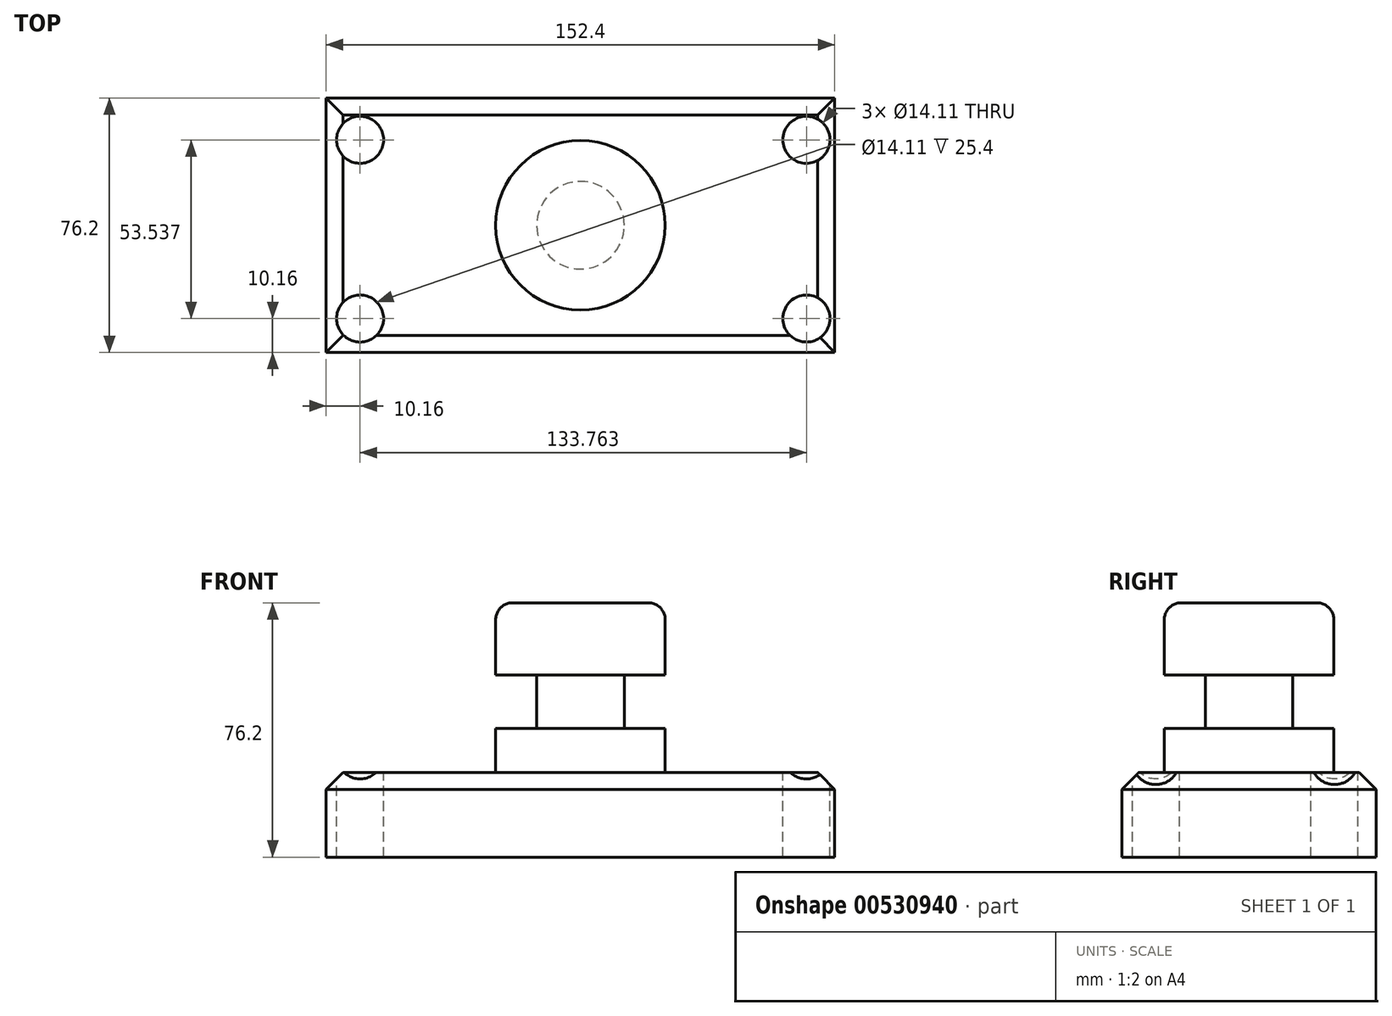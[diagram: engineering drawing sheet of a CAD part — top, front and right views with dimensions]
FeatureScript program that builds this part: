
annotation { "Feature Type Name" : "Feature", "Feature Type Description" : "" }
export const myFeature = defineFeature(function(context is Context, id is Id, definition is map)
    precondition{}
    {
        {
            var Q0;
            Q0=qCreatedBy(makeId("Top.planeOp"),FACE);
            var sketch = newSketch(context, id + "F0", { "sketchPlane" : qUnion([Q0])});
            skLineSegment(sketch, "E0.bottom", {"start": v(-76.2, 38.1) * mm, "end": v(76.2, 38.1) * mm});
            skLineSegment(sketch, "E0.top", {"start": v(-76.2, -38.1) * mm, "end": v(76.2, -38.1) * mm});
            skLineSegment(sketch, "E0.left", {"start": v(-76.2, 38.1) * mm, "end": v(-76.2, -38.1) * mm});
            skLineSegment(sketch, "E0.right", {"start": v(76.2, 38.1) * mm, "end": v(76.2, -38.1) * mm});
            skPoint(sketch, "E0.middle", {"position": v(0, 0) * mm});
            skSolve(sketch);
        }
        {
            var Q0;
            Q0=makeQuery(id+"F0.imprint","IMPRINT",FACE,{"disambiguationData":[TD([[makeQuery(id+"F0.imprint","IMPRINT",EDGE,{"derivedFrom":sQuery(id+"F0.wireOp",EDGE,"E0.bottom")}),-1.0]])]});
            extrude(context, id + "F1", {"entities" : qUnion([Q0]), "depth" : 25.4 * mm, "offsetDistance" : 25.4 * mm});
        }
        {
            var Q0;
            Q0=makeQuery(id+"F1.opExtrude","CAP_FACE",FACE,{"disambiguationData":[OSD([sQuery(id+"F0.wireOp",EDGE,"E0.bottom"),sQuery(id+"F0.wireOp",EDGE,"E0.top"),sQuery(id+"F0.wireOp",EDGE,"E0.left"),sQuery(id+"F0.wireOp",EDGE,"E0.right")])],"isStart":false});
            var sketch = newSketch(context, id + "F2", { "sketchPlane" : qUnion([Q0])});
            skCircle(sketch, "E1", {"center": v(67.72, 25.6) * mm, "radius": 7.05 * mm});
            skCircle(sketch, "E2", {"center": v(-66.04, 25.6) * mm, "radius": 7.05 * mm});
            skCircle(sketch, "E3", {"center": v(-66.04, -27.94) * mm, "radius": 7.05 * mm});
            skCircle(sketch, "E4", {"center": v(67.72, -27.94) * mm, "radius": 7.05 * mm});
            skSolve(sketch);
        }
        {
            var Q0;
            Q0 = qSketchRegion(id + "F2", true);
            extrude(context, id + "F3", {"entities" : qUnion([Q0]), "operationType" : NewBodyOperationType.REMOVE, "endBound" : BoundingType.THROUGH_ALL, "oppositeDirection" : true, "depth" : 25.4 * mm, "offsetDistance" : 25.4 * mm});
        }
        {
            var Q0;
            Q0=qCreatedBy(makeId("Front.planeOp"),FACE);
            var sketch = newSketch(context, id + "F4", { "sketchPlane" : qUnion([Q0])});
            skLineSegment(sketch, "E5.bottom", {"start": v(0, 25.4) * mm, "end": v(25.4, 25.4) * mm});
            skLineSegment(sketch, "E5.top", {"start": v(0, 76.2) * mm, "end": v(25.4, 76.2) * mm});
            skLineSegment(sketch, "E5.left", {"start": v(0, 25.4) * mm, "end": v(0, 76.2) * mm});
            skLineSegment(sketch, "E5.right", {"start": v(25.4, 25.4) * mm, "end": v(25.4, 76.2) * mm});
            skSolve(sketch);
        }
        {
            var Q0;
            Q0=makeQuery(id+"F4.imprint","IMPRINT",FACE,{"disambiguationData":[TD([[makeQuery(id+"F4.imprint","IMPRINT",EDGE,{"derivedFrom":sQuery(id+"F4.wireOp",EDGE,"E5.bottom")}),1.0]])]});
            var Q1;
            Q1=sQuery(id+"F4.wireOp",EDGE,"E5.left");
            revolve(context, id + "F5", {"operationType" : NewBodyOperationType.ADD, "entities" : qUnion([Q0]), "axis" : qUnion([Q1]), "revolveType" : RevolveType.FULL});
        }
        {
            var Q0;
            Q0=qCreatedBy(makeId("Front.planeOp"),FACE);
            var sketch = newSketch(context, id + "F6", { "sketchPlane" : qUnion([Q0])});
            skLineSegment(sketch, "E6.bottom", {"start": v(31.35, 54.56) * mm, "end": v(13.12, 54.56) * mm});
            skLineSegment(sketch, "E6.top", {"start": v(31.35, 38.53) * mm, "end": v(13.12, 38.53) * mm});
            skLineSegment(sketch, "E6.left", {"start": v(31.35, 54.56) * mm, "end": v(31.35, 38.53) * mm});
            skLineSegment(sketch, "E6.right", {"start": v(13.12, 54.56) * mm, "end": v(13.12, 38.53) * mm});
            skSolve(sketch);
        }
        {
            var Q0;
            Q0=qCreatedBy(makeId("Right.planeOp"),FACE);
            var sketch = newSketch(context, id + "F7", { "sketchPlane" : qUnion([Q0])});
            skLineSegment(sketch, "E7", {"start": v(0, 0) * mm, "end": v(0, 64.5) * mm});
            skSolve(sketch);
        }
        {
            var Q0;
            Q0 = qSketchRegion(id + "F6", true);
            var Q1;
            Q1=sQuery(id+"F7.wireOp",EDGE,"E7");
            revolve(context, id + "F8", {"operationType" : NewBodyOperationType.REMOVE, "entities" : qUnion([Q0]), "axis" : qUnion([Q1]), "revolveType" : RevolveType.FULL, "oppositeDirection" : true});
        }
        {
            var Q0;
            Q0=makeQuery(id+"F5.opRevolve","SWEPT_FACE",FACE,{"disambiguationData":[OSD([sQuery(id+"F4.wireOp",EDGE,"E5.top")])]});
            var Q1;
            Q1=makeQuery(id+"F5.opRevolve","SWEPT_EDGE",EDGE,{"disambiguationData":[OSD([sQuery(id+"F4.wireOp",EDGE,"E5.bottom"),sQuery(id+"F4.wireOp",EDGE,"E5.right")])]});
            fillet(context, id + "F9", {"entities" : qUnion([Q0, Q1]), "radius" : 5.08 * mm, "tangentPropagation" : true, "allowEdgeOverflow" : false});
        }
        {
            var Q0;
            Q0=makeQuery(id+"F1.opExtrude","CAP_EDGE",EDGE,{"disambiguationData":[OSD([sQuery(id+"F0.wireOp",EDGE,"E0.top")])],"isStart":false});
            var Q1;
            Q1=makeQuery(id+"F1.opExtrude","CAP_EDGE",EDGE,{"disambiguationData":[OSD([sQuery(id+"F0.wireOp",EDGE,"E0.right")])],"isStart":false});
            var Q2;
            Q2=makeQuery(id+"F1.opExtrude","CAP_EDGE",EDGE,{"disambiguationData":[OSD([sQuery(id+"F0.wireOp",EDGE,"E0.bottom")])],"isStart":false});
            var Q3;
            Q3=makeQuery(id+"F1.opExtrude","CAP_EDGE",EDGE,{"disambiguationData":[OSD([sQuery(id+"F0.wireOp",EDGE,"E0.left")])],"isStart":false});
            chamfer(context, id + "F10", {"entities" : qUnion([Q0, Q1, Q2, Q3]), "width" : 5.08 * mm, "tangentPropagation" : true});
        }
    });
